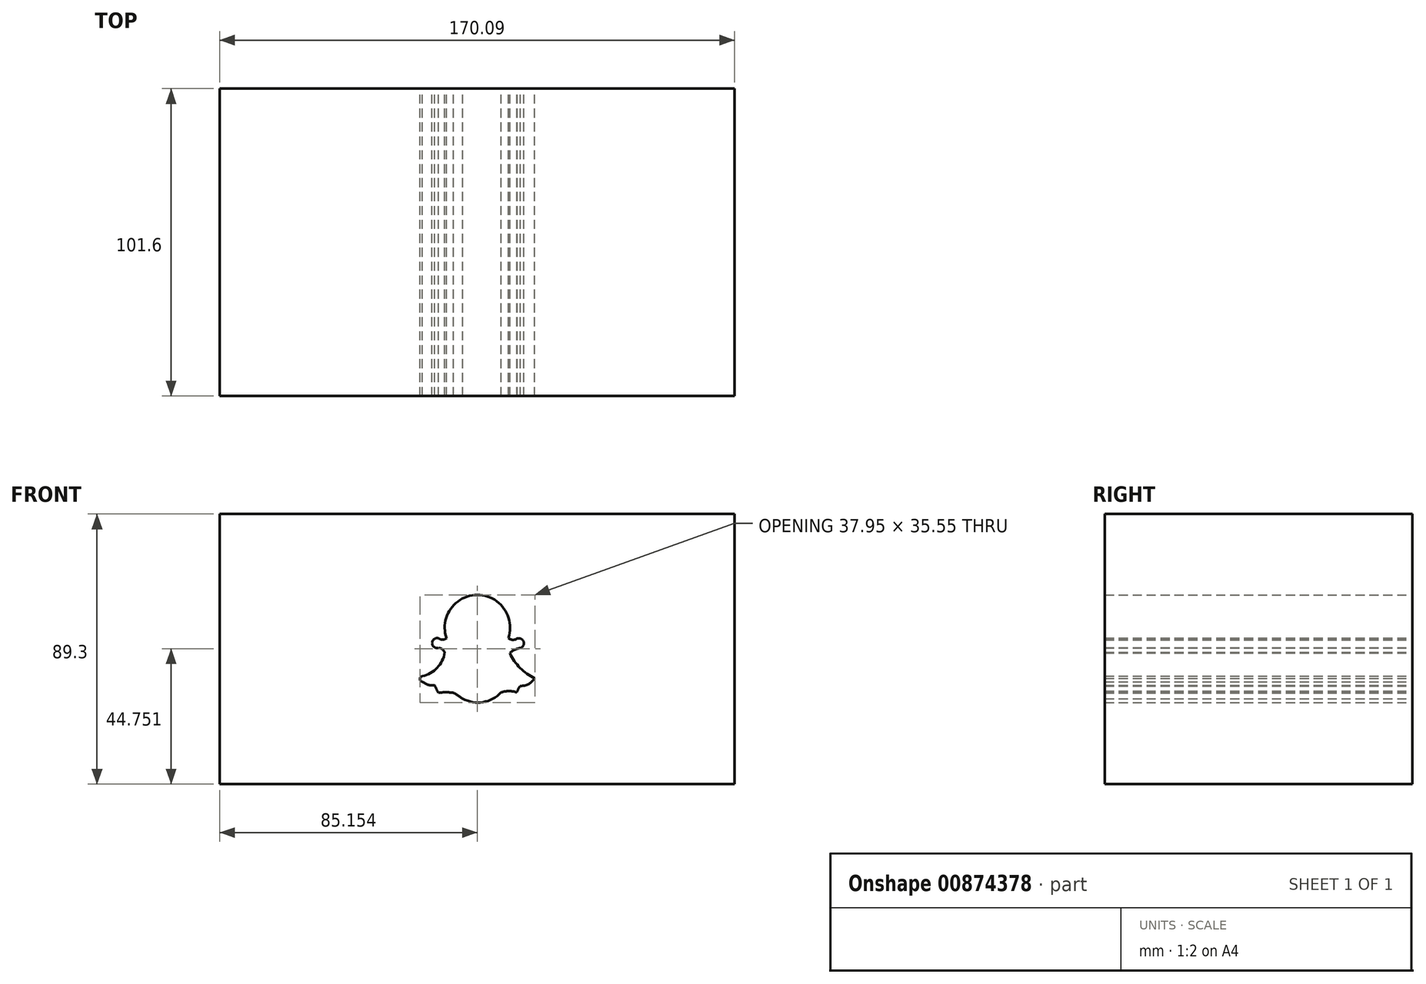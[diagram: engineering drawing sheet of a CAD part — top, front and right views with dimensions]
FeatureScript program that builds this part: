
annotation { "Feature Type Name" : "Feature", "Feature Type Description" : "" }
export const myFeature = defineFeature(function(context is Context, id is Id, definition is map)
    precondition{}
    {
        {
            var Q0;
            Q0=qCreatedBy(makeId("Front.planeOp"),FACE);
            var sketch = newSketch(context, id + "F0", { "sketchPlane" : qUnion([Q0])});
            skArc(sketch, "E0", {"start": v(95.42, 48.3) * mm, "mid": v(85.13, 62.53) * mm, "end": v(74.95, 48.21) * mm});
            skArc(sketch, "E1", {"start": v(72.33, 48.21) * mm, "mid": v(73.64, 47.77) * mm, "end": v(74.95, 48.21) * mm});
            skArc(sketch, "E2", {"start": v(72.33, 48.21) * mm, "mid": v(70.21, 46.65) * mm, "end": v(72.33, 45.08) * mm});
            skArc(sketch, "E3", {"start": v(74.36, 43.56) * mm, "mid": v(73.55, 44.6) * mm, "end": v(72.33, 45.08) * mm});
            skArc(sketch, "E4", {"start": v(67, 35.7) * mm, "mid": v(71.9, 38.5) * mm, "end": v(74.36, 43.56) * mm});
            skArc(sketch, "E5", {"start": v(67, 35.7) * mm, "mid": v(66.18, 34.77) * mm, "end": v(67, 33.84) * mm});
            skArc(sketch, "E6", {"start": v(67, 33.84) * mm, "mid": v(68.92, 32.86) * mm, "end": v(71.06, 32.65) * mm});
            skArc(sketch, "E7", {"start": v(71.06, 32.65) * mm, "mid": v(71.64, 31.42) * mm, "end": v(72.25, 30.2) * mm});
            skArc(sketch, "E8", {"start": v(77.32, 30.2) * mm, "mid": v(74.79, 30.38) * mm, "end": v(72.25, 30.2) * mm});
            skArc(sketch, "E9", {"start": v(80.28, 28.26) * mm, "mid": v(78.8, 29.24) * mm, "end": v(77.32, 30.2) * mm});
            skArc(sketch, "E10", {"start": v(80.28, 28.26) * mm, "mid": v(87.03, 27.12) * mm, "end": v(93.05, 30.37) * mm});
            skArc(sketch, "E11", {"start": v(98.2, 30.37) * mm, "mid": v(95.63, 30.75) * mm, "end": v(93.05, 30.37) * mm});
            skArc(sketch, "E12", {"start": v(99.4, 32.49) * mm, "mid": v(98.7, 31.49) * mm, "end": v(98.2, 30.37) * mm});
            skArc(sketch, "E13", {"start": v(99.4, 32.49) * mm, "mid": v(102.1, 33.11) * mm, "end": v(104.13, 35.02) * mm});
            skArc(sketch, "E14", {"start": v(95.93, 43.3) * mm, "mid": v(99.28, 38.42) * mm, "end": v(104.13, 35.02) * mm});
            skArc(sketch, "E15", {"start": v(99.4, 45) * mm, "mid": v(97.52, 44.44) * mm, "end": v(95.93, 43.3) * mm});
            skArc(sketch, "E16", {"start": v(99.4, 45) * mm, "mid": v(100.42, 47.12) * mm, "end": v(98.3, 48.13) * mm});
            skArc(sketch, "E17", {"start": v(95.42, 48.3) * mm, "mid": v(96.83, 47.7) * mm, "end": v(98.3, 48.13) * mm});
            skLineSegment(sketch, "E18", {"start": v(170.1, 89.3) * mm, "end": v(170.1, 0) * mm});
            skLineSegment(sketch, "E19", {"start": v(170.1, 0) * mm, "end": v(0, 0) * mm});
            skLineSegment(sketch, "E20", {"start": v(0, 0) * mm, "end": v(0, 89.3) * mm});
            skLineSegment(sketch, "E21", {"start": v(170.1, 89.3) * mm, "end": v(0, 89.3) * mm});
            skSolve(sketch);
        }
        {
            var Q0;
            Q0=makeQuery(id+"F0.imprint","IMPRINT",FACE,{"disambiguationData":[TD([[makeQuery(id+"F0.imprint","IMPRINT",EDGE,{"derivedFrom":sQuery(id+"F0.wireOp",EDGE,"E0")}),-1.0]])]});
            extrude(context, id + "F1", {"entities" : qUnion([Q0]), "depth" : 25.4 * mm, "offsetDistance" : 25.4 * mm});
        }
        {
            var Q0;
            Q0=makeQuery(id+"F1.opExtrude","CAP_FACE",FACE,{"disambiguationData":[OSD([sQuery(id+"F0.wireOp",EDGE,"E0"),sQuery(id+"F0.wireOp",EDGE,"E1"),sQuery(id+"F0.wireOp",EDGE,"E2"),sQuery(id+"F0.wireOp",EDGE,"E3"),sQuery(id+"F0.wireOp",EDGE,"E4"),sQuery(id+"F0.wireOp",EDGE,"E5"),sQuery(id+"F0.wireOp",EDGE,"E6"),sQuery(id+"F0.wireOp",EDGE,"E7"),sQuery(id+"F0.wireOp",EDGE,"E8"),sQuery(id+"F0.wireOp",EDGE,"E9"),sQuery(id+"F0.wireOp",EDGE,"E10"),sQuery(id+"F0.wireOp",EDGE,"E11"),sQuery(id+"F0.wireOp",EDGE,"E12"),sQuery(id+"F0.wireOp",EDGE,"E13"),sQuery(id+"F0.wireOp",EDGE,"E14"),sQuery(id+"F0.wireOp",EDGE,"E15"),sQuery(id+"F0.wireOp",EDGE,"E16"),sQuery(id+"F0.wireOp",EDGE,"E17"),sQuery(id+"F0.wireOp",EDGE,"E18"),sQuery(id+"F0.wireOp",EDGE,"E19"),sQuery(id+"F0.wireOp",EDGE,"E20"),sQuery(id+"F0.wireOp",EDGE,"E21")])],"isStart":false});
            extrude(context, id + "F2", {"entities" : qUnion([Q0]), "operationType" : NewBodyOperationType.ADD, "depth" : 76.2 * mm, "offsetDistance" : 25.4 * mm});
        }
    });
